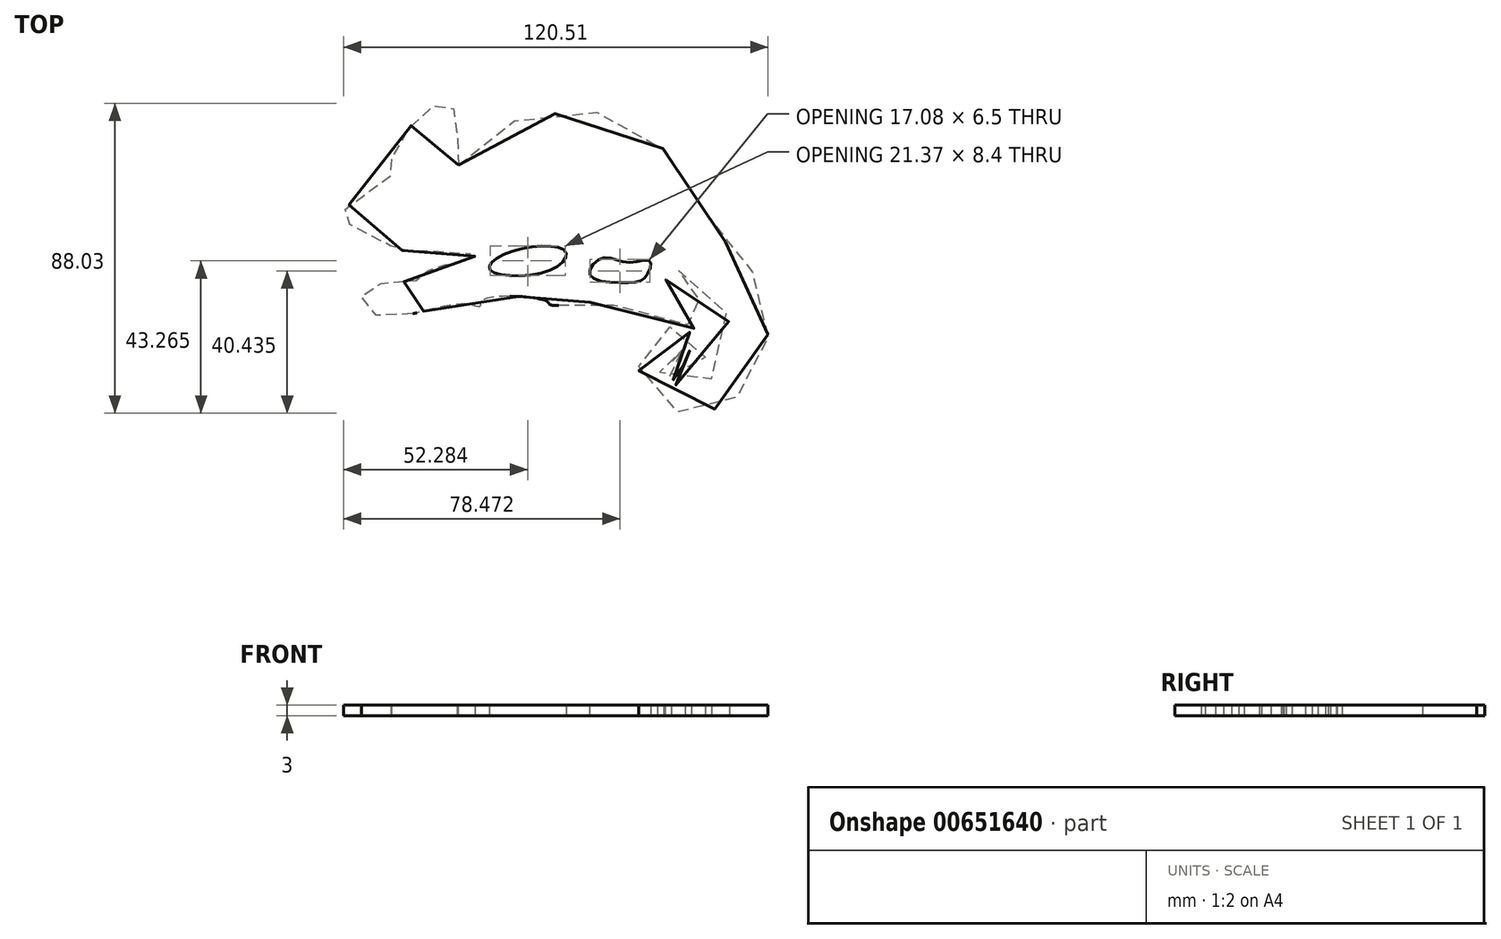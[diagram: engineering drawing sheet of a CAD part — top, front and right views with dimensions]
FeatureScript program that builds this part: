
annotation { "Feature Type Name" : "Feature", "Feature Type Description" : "" }
export const myFeature = defineFeature(function(context is Context, id is Id, definition is map)
    precondition{}
    {
        {
            var Q0;
            Q0=qCreatedBy(makeId("Top.planeOp"),FACE);
            var sketch = newSketch(context, id + "F0", { "sketchPlane" : qUnion([Q0])});
            skFitSpline(sketch, "E0", {"points": [v(-32.36, 10.74) * mm, v(-25.01, 18.63) * mm, v(-7.62, 25.09) * mm, v(9.77, 25.27) * mm, v(23.58, 17.56) * mm, v(34.52, 3.93) * mm, v(40.8, -7.9) * mm, v(50.83, -19.2) * mm, v(54.78, -30.32) * mm, v(54.78, -43.23) * mm, v(47.96, -53.99) * mm, v(40.61, -58.47) * mm, v(28.96, -59.18) * mm, v(20.17, -52.55) * mm, v(19.63, -42.33) * mm, v(25.01, -35.52) * mm, v(29.5, -35.52) * mm, v(35.77, -38.39) * mm, v(37.56, -45.74) * mm, v(33.08, -50.94) * mm, v(26.98, -48.96) * mm, v(26.27, -43.94) * mm, v(29.5, -41.61) * mm, v(31.83, -42.87) * mm, v(31.47, -45.92) * mm, v(29.85, -43.59) * mm, v(28.06, -45.74) * mm, v(32, -48.07) * mm, v(33.26, -41.97) * mm, v(28.24, -40.18) * mm, v(24.3, -44.48) * mm, v(26.8, -50.4) * mm, v(36.13, -51.83) * mm, v(42.58, -45.2) * mm, v(43.84, -31.57) * mm, v(36.49, -24.04) * mm, v(28.6, -19.2) * mm, v(26.98, -24.94) * mm, v(39.18, -29.06) * mm, v(35.95, -35.52) * mm, v(31.65, -33.9) * mm, v(16.05, -29.78) * mm, v(2.42, -28.17) * mm, v(-2.42, -28.88) * mm, v(-6.37, -28.88) * mm, v(-7.44, -27.8) * mm, v(-25.55, -27.63) * mm, v(-26.27, -29.42) * mm, v(-31.47, -28.7) * mm, v(-56.21, -31.75) * mm, v(-59.08, -24.58) * mm, v(-42.4, -21.35) * mm, v(-40.61, -18.66) * mm, v(-32.18, -17.05) * mm, v(-27.7, -14.9) * mm, v(-34.52, -14.18) * mm, v(-39.72, -13.64) * mm, v(-47.6, -13.64) * mm, v(-54.6, -10.6) * mm, v(-63.38, -5.93) * mm, v(-64.46, -1.63) * mm, v(-51.9, 7.34) * mm, v(-51.55, 11.46) * mm, v(-39.9, 27.42) * mm, v(-33.26, 25.62) * mm, v(-32.36, 10.74) * mm]});
            skFitSpline(sketch, "E1", {"points": [v(-23.4, -19.02) * mm, v(-18.02, -14) * mm, v(-2.06, -13.64) * mm, v(-6.19, -19.02) * mm, v(-23.4, -19.02) * mm]});
            skFitSpline(sketch, "E2", {"points": [v(4.93, -20.46) * mm, v(8.52, -15.61) * mm, v(15.5, -16.87) * mm, v(21.96, -16.51) * mm, v(20.89, -20.81) * mm, v(15.69, -22.6) * mm, v(4.93, -20.46) * mm]});
            skSolve(sketch);
        }
        {
            var Q0;
            Q0=makeQuery(id+"F0.imprint","IMPRINT",FACE,{"disambiguationData":[TD([[makeQuery(id+"F0.imprint","IMPRINT",EDGE,{"derivedFrom":sQuery(id+"F0.wireOp",EDGE,"E0")}),-1.0]])]});
            extrude(context, id + "F1", {"entities" : qUnion([Q0]), "depth" : 3 * mm, "offsetDistance" : 25.4 * mm});
        }
    });
